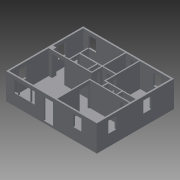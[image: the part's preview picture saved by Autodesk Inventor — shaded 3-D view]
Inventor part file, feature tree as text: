
AUTODESK INVENTOR PART (.ipt)
format: ipt  version: 2013 (Build 170138000, 138)  size: 411,136 bytes
history: native  units: in
note: dims shown in document units (in); Inventor stores cm internally (conversion verified against a paired STEP export)
features: extrude x11, sketch x10
ambient origin geometry x8: Origin, YZ Plane, XZ Plane, XY Plane, X Axis, Y Axis, Z Axis, Center Point
feature tree (21):
  extrude  "Extrusion8"  Depth=360.0in
  extrude  "Extrusion11"  Depth=340.0in
  extrude  "Extrusion12"  Depth=28.0in
  extrude  "Extrusion13"  Depth=4.0in
  extrude  "Extrusion14"  Depth=28.0in
  extrude  "Extrusion15"  Depth=4.5in
  extrude  "Extrusion16"  Depth=4.0in
  extrude  "Extrusion17"  Depth=28.0in
  extrude  "Extrusion18"  Depth=164.0in
  sketch  "Sketch18"  dims[d34=150.0in d35=36.0in d36=157.0in d40=4.5in d41=31.5in d42=4.5in d44=12.0in d46=60.0in d48=4.5in d52=4.5in d60=157.0in d61=4.5in d117=6.0in d118=6.0in d119=6.0in d120=6.0in d121=6.0in d122=6.0in d123=6.0in d124=4.5in d125=4.5in d126=4.5in d127=4.5in d128=4.5in d129=4.5in d130=4.5in d131=4.5in d133=4.5in d134=4.5in d135=6.0in d138=6.0in d139=135.0in d140=129.0in d141=129.0in d142=157.0in d148=166.0in d149=4.5in d154=18.0in d155=10.0in d160=13.5in d161=4.5in d162=52.0in d164=12.0in d165=52.0in d166=6.0in d170=4.5in d172=36.0in d173=6.0in d174=36.0in d175=4.5in d176=4.5in d177=122.0in d178=96.0in d179=0.0in d184=14.0in d185=46.0in d186=31.0in d187=45.0in d188=45.0in d189=31.0in d190=90.0in d191=6.0in d192=0.0in d193=62.0in d194=31.0in d195=45.0in d196=47.0in d197=85.0in d199=19.0in d200=30.5in d203=2.0in d204=2.0in d205=0.0in d206=0.0in d207=0.0in d208=0.0in d209=2.0in d210=2.0in d211=6.0in d212=0.0in d213=14.0in d214=31.0in d215=31.0in d216=45.0in d217=43.5in d218=75.0in d219=6.0in d220=0.0in d221=30.0in d223=14.0in d224=45.0in d225=27.0in d226=30.0in d227=45.0in d228=16.0in d229=26.0in d230=150.0in d231=6.0in d232=0.0in d238=154.0in d241=137.0in d242=38.0in d243=48.0in d246=17.5in d247=67.5in d248=38.0in d249=4.5in d250=96.0in d251=0.0in d252=14.0in d253=14.0in d254=0.0in d255=8.0in d256=0.0in d257=14.0in d258=0.0in d259=4.5in d260=4.5in d261=14.0in d262=0.0in d263=96.0in d264=0.0in]
  extrude  "Extrusion19"  Depth=36.0in
  extrude  "Extrusion20"  Depth=157.0in
  sketch  "Sketch1"  dims[d0=306.0in d2=360.0in]
  sketch  "Sketch10"  dims[d3=294.0in d4=340.0in]
  sketch  "Sketch11"  dims[d7=4.0in d8=4.0in d9=129.0in d11=28.0in]
  sketch  "Sketch12"  dims[d13=135.0in d14=122.0in d15=4.0in d16=4.0in]
  sketch  "Sketch13"  dims[d18=44.0in d19=28.0in]
  sketch  "Sketch14"  dims[d21=4.5in d22=4.5in]
  sketch  "Sketch15"  dims[d23=129.0in d26=4.0in d27=4.0in]
  sketch  "Sketch16"  dims[d28=4.0in d29=28.0in]
  sketch  "Sketch17"  dims[d30=166.0in d33=164.0in]
